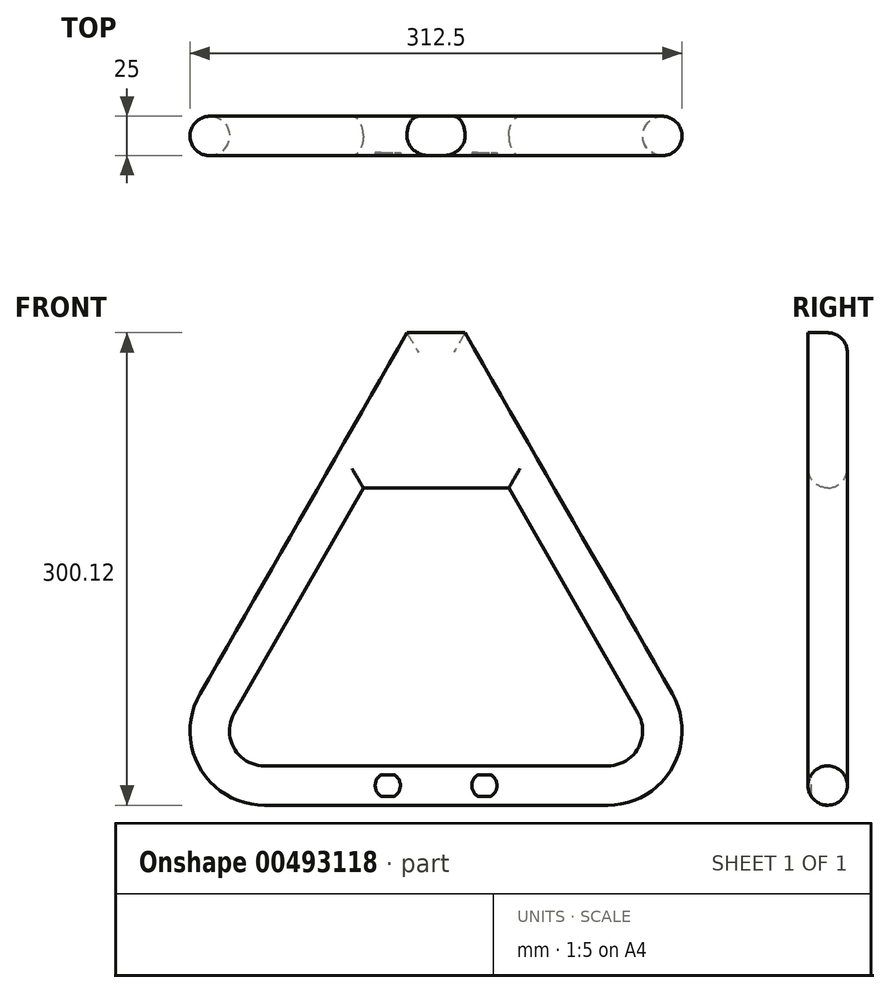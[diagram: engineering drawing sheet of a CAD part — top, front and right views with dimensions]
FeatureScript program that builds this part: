
annotation { "Feature Type Name" : "Feature", "Feature Type Description" : "" }
export const myFeature = defineFeature(function(context is Context, id is Id, definition is map)
    precondition{}
    {
        {
            var Q0;
            Q0=qCreatedBy(makeId("Front.planeOp"),FACE);
            var sketch = newSketch(context, id + "F0", { "sketchPlane" : qUnion([Q0])});
            skLineSegment(sketch, "E0", {"start": v(-46.19, 46) * mm, "end": v(46.19, 46) * mm});
            skLineSegment(sketch, "E1", {"start": v(46.19, 46) * mm, "end": v(128.31, -97.26) * mm});
            skLineSegment(sketch, "E2", {"start": v(-128.31, -97.26) * mm, "end": v(-46.19, 46) * mm});
            skLineSegment(sketch, "E3", {"start": v(-39.68, 82.48) * mm, "end": v(-128.31, -72.13) * mm, "construction": true});
            skLineSegment(sketch, "E4", {"start": v(40.08, 81.8) * mm, "end": v(151.31, -112.25) * mm, "construction": true});
            skArc(sketch, "E5", {"start": v(-128.31, -97.26) * mm, "mid": v(-128.26, -119.46) * mm, "end": v(-109.03, -130.54) * mm});
            skArc(sketch, "E6", {"start": v(109.03, -130.54) * mm, "mid": v(128.26, -119.46) * mm, "end": v(128.31, -97.26) * mm});
            skLineSegment(sketch, "E7", {"start": v(-18.5, 144.58) * mm, "end": v(18.5, 144.58) * mm});
            skLineSegment(sketch, "E8", {"start": v(18.5, 144.58) * mm, "end": v(150, -84.83) * mm});
            skLineSegment(sketch, "E9", {"start": v(-18.5, 144.58) * mm, "end": v(-150, -84.83) * mm});
            skLineSegment(sketch, "E10", {"start": v(-109.03, -155.54) * mm, "end": v(109.03, -155.54) * mm});
            skArc(sketch, "E11", {"start": v(-150, -84.83) * mm, "mid": v(-149.9, -131.99) * mm, "end": v(-109.03, -155.54) * mm});
            skArc(sketch, "E12", {"start": v(109.03, -155.54) * mm, "mid": v(149.9, -131.99) * mm, "end": v(150, -84.83) * mm});
            skLineSegment(sketch, "E13", {"start": v(-109.03, -130.54) * mm, "end": v(109.03, -130.54) * mm});
            skSolve(sketch);
        }
        {
            var Q0;
            Q0 = qSketchRegion(id + "F0", true);
            extrude(context, id + "F1", {"entities" : qUnion([Q0]), "depth" : 25 * mm});
        }
        {
            var Q0;
            Q0=makeQuery(id+"F1.opExtrude","CAP_EDGE",EDGE,{"disambiguationData":[OSD([sQuery(id+"F0.wireOp",EDGE,"E2")])],"isStart":false});
            var Q1;
            Q1=makeQuery(id+"F1.opExtrude","CAP_EDGE",EDGE,{"disambiguationData":[OSD([sQuery(id+"F0.wireOp",EDGE,"E0")])],"isStart":false});
            var Q2;
            Q2=makeQuery(id+"F1.opExtrude","CAP_EDGE",EDGE,{"disambiguationData":[OSD([sQuery(id+"F0.wireOp",EDGE,"E1")])],"isStart":false});
            var Q3;
            Q3=makeQuery(id+"F1.opExtrude","CAP_EDGE",EDGE,{"disambiguationData":[OSD([sQuery(id+"F0.wireOp",EDGE,"E6")])],"isStart":false});
            var Q4;
            Q4=makeQuery(id+"F1.opExtrude","CAP_EDGE",EDGE,{"disambiguationData":[OSD([sQuery(id+"F0.wireOp",EDGE,"oOzAJNuk-MyMY-iwTg-xMS7-AM1MQOvxiyRB")])],"isStart":false});
            var Q5;
            Q5=makeQuery(id+"F1.opExtrude","CAP_EDGE",EDGE,{"disambiguationData":[OSD([sQuery(id+"F0.wireOp",EDGE,"E5")])],"isStart":false});
            fillet(context, id + "F2", {"entities" : qUnion([Q0, Q1, Q2, Q3, Q4, Q5]), "radius" : 12.5 * mm, "tangentPropagation" : true, "allowEdgeOverflow" : false});
        }
        {
            var Q0;
            Q0=makeQuery(id+"F1.opExtrude","CAP_EDGE",EDGE,{"disambiguationData":[OSD([sQuery(id+"F0.wireOp",EDGE,"E9")])],"isStart":false});
            var Q1;
            Q1=makeQuery(id+"F1.opExtrude","CAP_EDGE",EDGE,{"disambiguationData":[OSD([sQuery(id+"F0.wireOp",EDGE,"E8")])],"isStart":false});
            var Q2;
            Q2=makeQuery(id+"F1.opExtrude","CAP_EDGE",EDGE,{"disambiguationData":[OSD([sQuery(id+"F0.wireOp",EDGE,"E11")])],"isStart":false});
            fillet(context, id + "F3", {"entities" : qUnion([Q0, Q1, Q2]), "radius" : 12.5 * mm, "tangentPropagation" : true, "allowEdgeOverflow" : false});
        }
        {
            var Q0;
            Q0=qCreatedBy(makeId("Front.planeOp"),FACE);
            cPlane(context, id + "F4", {"entities" : qUnion([Q0]), "cplaneType" : CPlaneType.OFFSET, "offset" : 25 * mm, "width" : 150 * mm, "height" : 150 * mm});
        }
        {
            var Q0;
            Q0=qCreatedBy(id+"F4.planeOp",FACE);
            var sketch = newSketch(context, id + "F5", { "sketchPlane" : qUnion([Q0])});
            skCircle(sketch, "E14", {"center": v(-30.67, -143.04) * mm, "radius": 8 * mm});
            skCircle(sketch, "E15", {"center": v(30.67, -143.04) * mm, "radius": 8 * mm});
            skSolve(sketch);
        }
        {
            var Q0;
            Q0 = qSketchRegion(id + "F5", true);
            extrude(context, id + "F6", {"entities" : qUnion([Q0]), "operationType" : NewBodyOperationType.REMOVE, "oppositeDirection" : true, "depth" : 2 * mm});
        }
        {
            var Q0;
            Q0=makeQuery(id+"F1.opExtrude","CAP_FACE",FACE,{"disambiguationData":[OSD([sQuery(id+"F0.wireOp",EDGE,"E0"),sQuery(id+"F0.wireOp",EDGE,"E1"),sQuery(id+"F0.wireOp",EDGE,"E2"),sQuery(id+"F0.wireOp",EDGE,"E5"),sQuery(id+"F0.wireOp",EDGE,"E6"),sQuery(id+"F0.wireOp",EDGE,"E7"),sQuery(id+"F0.wireOp",EDGE,"E8"),sQuery(id+"F0.wireOp",EDGE,"E9"),sQuery(id+"F0.wireOp",EDGE,"E10"),sQuery(id+"F0.wireOp",EDGE,"E11"),sQuery(id+"F0.wireOp",EDGE,"E12"),sQuery(id+"F0.wireOp",EDGE,"E13")])],"isStart":true});
            fillet(context, id + "F7", {"entities" : qUnion([Q0]), "radius" : 12.5 * mm, "tangentPropagation" : true, "allowEdgeOverflow" : false});
        }
    });
